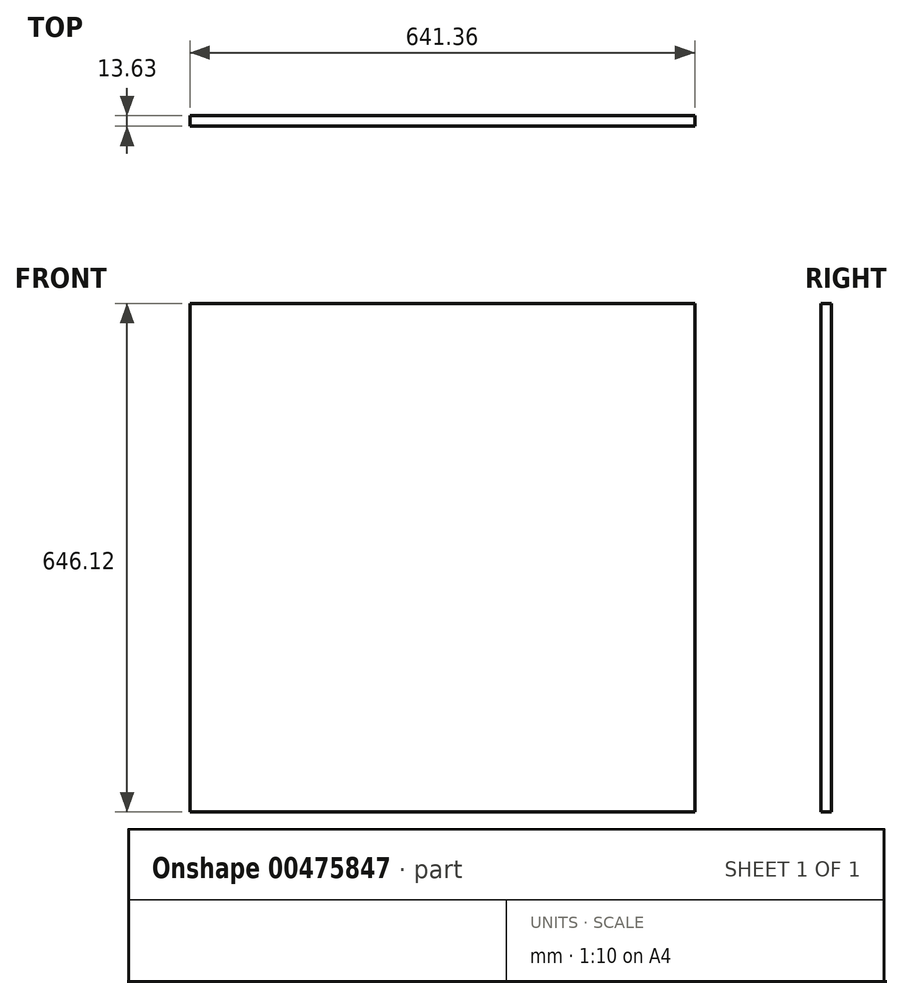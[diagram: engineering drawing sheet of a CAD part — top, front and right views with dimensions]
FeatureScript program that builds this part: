
annotation { "Feature Type Name" : "Feature", "Feature Type Description" : "" }
export const myFeature = defineFeature(function(context is Context, id is Id, definition is map)
    precondition{}
    {
        {
            var Q0;
            Q0=qCreatedBy(makeId("Front.planeOp"),FACE);
            var sketch = newSketch(context, id + "F0", { "sketchPlane" : qUnion([Q0])});
            skLineSegment(sketch, "E0.bottom", {"start": v(320.68, -323.06) * mm, "end": v(-320.68, -323.06) * mm});
            skLineSegment(sketch, "E0.top", {"start": v(320.68, 323.06) * mm, "end": v(-320.68, 323.06) * mm});
            skLineSegment(sketch, "E0.left", {"start": v(320.68, -323.06) * mm, "end": v(320.68, 323.06) * mm});
            skLineSegment(sketch, "E0.right", {"start": v(-320.68, -323.06) * mm, "end": v(-320.68, 323.06) * mm});
            skPoint(sketch, "E0.middle", {"position": v(0, 0) * mm});
            skSolve(sketch);
        }
        {
            var Q0;
            Q0=makeQuery(id+"F0.imprint","IMPRINT",FACE,{"disambiguationData":[TD([[makeQuery(id+"F0.imprint","IMPRINT",EDGE,{"derivedFrom":sQuery(id+"F0.wireOp",EDGE,"E0.bottom")}),-1.0]])]});
            extrude(context, id + "F1", {"entities" : qUnion([Q0]), "depth" : 13.63 * mm});
        }
    });
